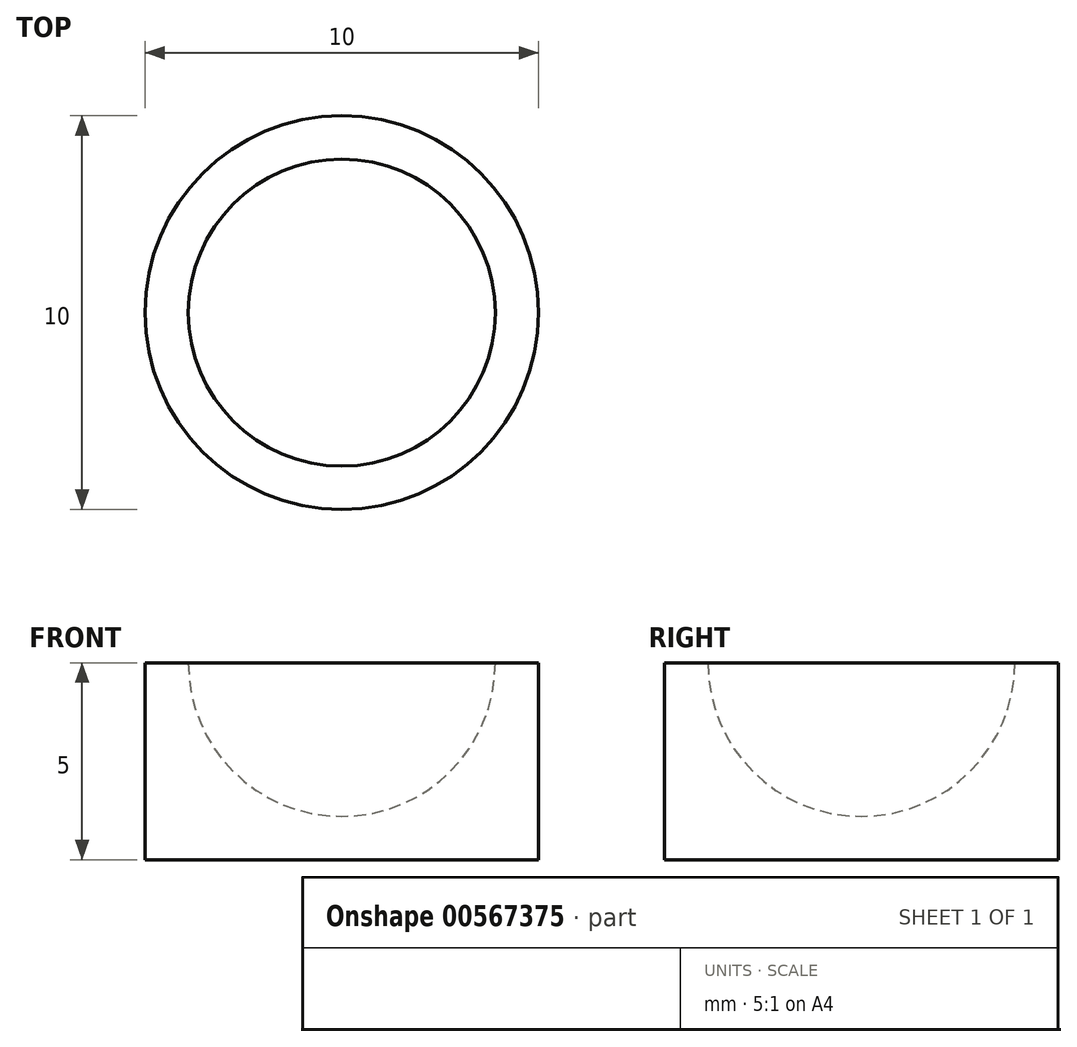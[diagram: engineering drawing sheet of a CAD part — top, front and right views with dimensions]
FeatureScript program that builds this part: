
annotation { "Feature Type Name" : "Feature", "Feature Type Description" : "" }
export const myFeature = defineFeature(function(context is Context, id is Id, definition is map)
    precondition{}
    {
        {
            var Q0;
            Q0=qCreatedBy(makeId("Top.planeOp"),FACE);
            var sketch = newSketch(context, id + "F0", { "sketchPlane" : qUnion([Q0])});
            skCircle(sketch, "E0", {"center": v(0, 0) * mm, "radius": 5 * mm});
            skSolve(sketch);
        }
        {
            var Q0;
            Q0 = qSketchRegion(id + "F0", true);
            extrude(context, id + "F1", {"entities" : qUnion([Q0]), "oppositeDirection" : true, "depth" : 5 * mm, "offsetDistance" : 25 * mm});
        }
        {
            var Q0;
            Q0=makeQuery(id+"F1.opExtrude","CAP_FACE",FACE,{"disambiguationData":[OSD([sQuery(id+"F0.wireOp",EDGE,"E0")])],"isStart":true});
            var sketch = newSketch(context, id + "F2", { "sketchPlane" : qUnion([Q0])});
            skArc(sketch, "E1", {"start": v(3.9, 0) * mm, "mid": v(0, 3.9) * mm, "end": v(-3.9, 0) * mm});
            skLineSegment(sketch, "E2", {"start": v(-3.9, 0) * mm, "end": v(3.9, 0) * mm});
            skSolve(sketch);
        }
        {
            var Q0;
            Q0 = qSketchRegion(id + "F2", true);
            var Q1;
            Q1=sQuery(id+"F2.wireOp",EDGE,"E2");
            revolve(context, id + "F3", {"operationType" : NewBodyOperationType.REMOVE, "entities" : qUnion([Q0]), "axis" : qUnion([Q1]), "revolveType" : RevolveType.FULL, "oppositeDirection" : true});
        }
    });
